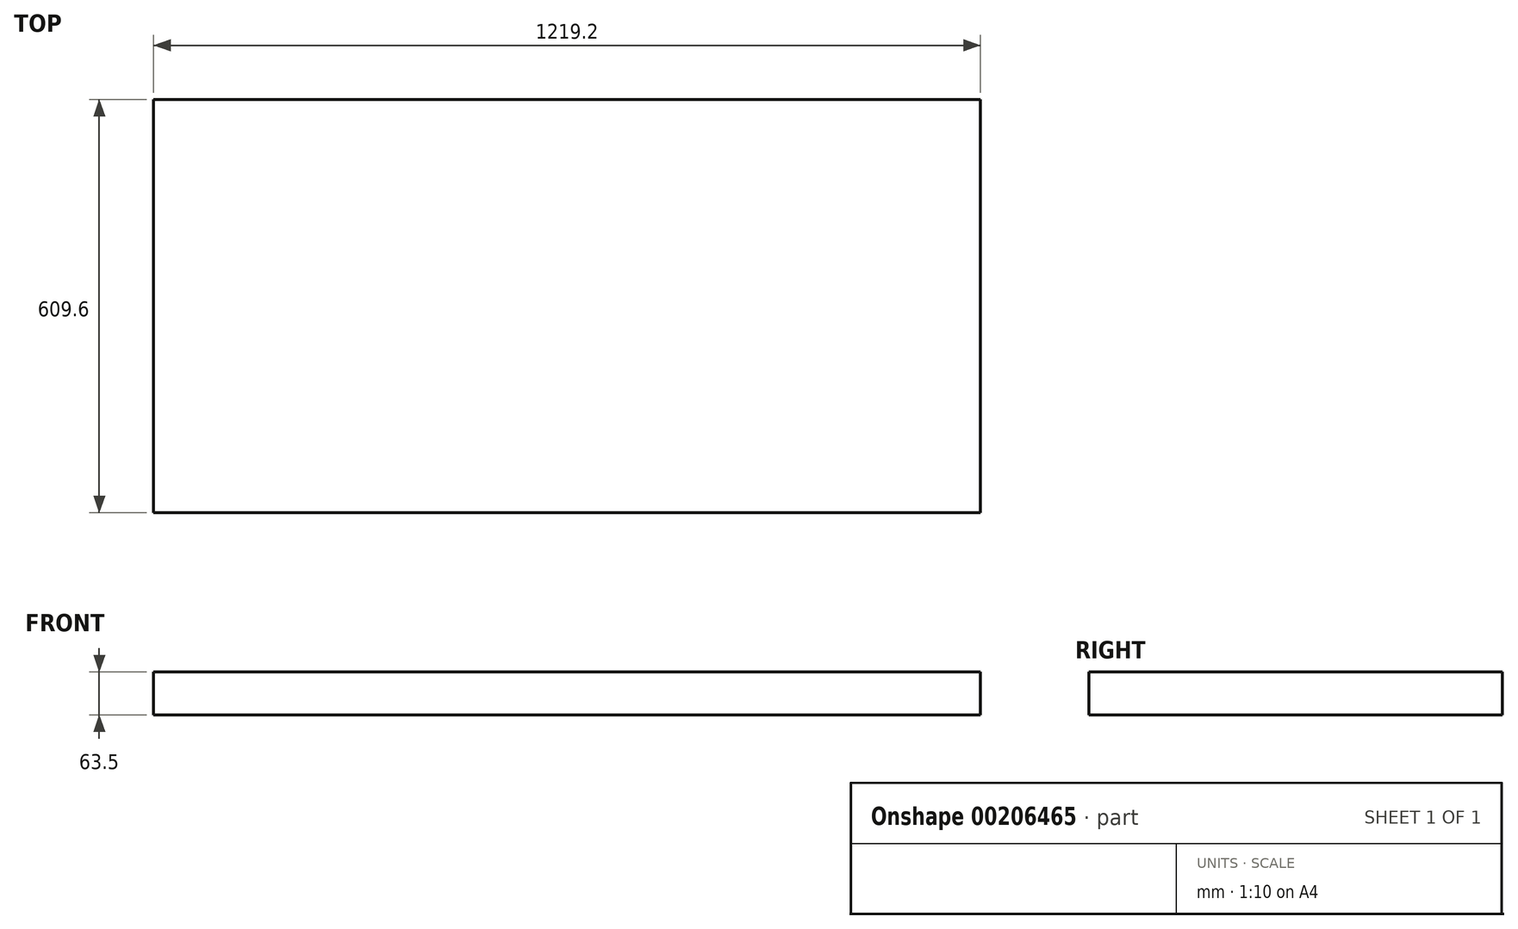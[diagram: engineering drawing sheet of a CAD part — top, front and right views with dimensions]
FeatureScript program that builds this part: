
annotation { "Feature Type Name" : "Feature", "Feature Type Description" : "" }
export const myFeature = defineFeature(function(context is Context, id is Id, definition is map)
    precondition{}
    {
        {
            var Q0;
            Q0=qCreatedBy(makeId("Top.planeOp"),FACE);
            var sketch = newSketch(context, id + "F0", { "sketchPlane" : qUnion([Q0])});
            skLineSegment(sketch, "E0.bottom", {"start": v(609.6, 304.8) * mm, "end": v(-609.6, 304.8) * mm});
            skLineSegment(sketch, "E0.top", {"start": v(609.6, -304.8) * mm, "end": v(-609.6, -304.8) * mm});
            skLineSegment(sketch, "E0.left", {"start": v(609.6, 304.8) * mm, "end": v(609.6, -304.8) * mm});
            skLineSegment(sketch, "E0.right", {"start": v(-609.6, 304.8) * mm, "end": v(-609.6, -304.8) * mm});
            skPoint(sketch, "E0.middle", {"position": v(0, 0) * mm});
            skLineSegment(sketch, "E1.bottom", {"start": v(-609.6, -304.8) * mm, "end": v(-457.2, -304.8) * mm});
            skLineSegment(sketch, "E1.top", {"start": v(-609.6, -152.4) * mm, "end": v(-457.2, -152.4) * mm});
            skLineSegment(sketch, "E1.left", {"start": v(-609.6, -304.8) * mm, "end": v(-609.6, -152.4) * mm});
            skLineSegment(sketch, "E1.right", {"start": v(-457.2, -304.8) * mm, "end": v(-457.2, -152.4) * mm});
            skLineSegment(sketch, "E2.bottom", {"start": v(-609.6, 304.8) * mm, "end": v(-457.2, 304.8) * mm});
            skLineSegment(sketch, "E2.top", {"start": v(-609.6, 152.4) * mm, "end": v(-457.2, 152.4) * mm});
            skLineSegment(sketch, "E2.left", {"start": v(-609.6, 304.8) * mm, "end": v(-609.6, 152.4) * mm});
            skLineSegment(sketch, "E2.right", {"start": v(-457.2, 304.8) * mm, "end": v(-457.2, 152.4) * mm});
            skLineSegment(sketch, "E3.bottom", {"start": v(609.6, 304.8) * mm, "end": v(457.2, 304.8) * mm});
            skLineSegment(sketch, "E3.top", {"start": v(609.6, 152.4) * mm, "end": v(457.2, 152.4) * mm});
            skLineSegment(sketch, "E3.left", {"start": v(609.6, 304.8) * mm, "end": v(609.6, 152.4) * mm});
            skLineSegment(sketch, "E3.right", {"start": v(457.2, 304.8) * mm, "end": v(457.2, 152.4) * mm});
            skLineSegment(sketch, "E4.bottom", {"start": v(609.6, -304.8) * mm, "end": v(457.2, -304.8) * mm});
            skLineSegment(sketch, "E4.top", {"start": v(609.6, -152.4) * mm, "end": v(457.2, -152.4) * mm});
            skLineSegment(sketch, "E4.left", {"start": v(609.6, -304.8) * mm, "end": v(609.6, -152.4) * mm});
            skLineSegment(sketch, "E4.right", {"start": v(457.2, -304.8) * mm, "end": v(457.2, -152.4) * mm});
            skPoint(sketch, "E5", {"position": v(-533.4, -228.6) * mm});
            skPoint(sketch, "E5.positionSnap0", {"position": v(-457.2, -228.6) * mm});
            skPoint(sketch, "E5.positionSnap1", {"position": v(-533.4, -152.4) * mm});
            skPoint(sketch, "E6", {"position": v(-533.4, 228.6) * mm});
            skPoint(sketch, "E6.positionSnap0", {"position": v(-533.4, 304.8) * mm});
            skPoint(sketch, "E6.positionSnap1", {"position": v(-457.2, 228.6) * mm});
            skPoint(sketch, "E7", {"position": v(533.4, 228.6) * mm});
            skPoint(sketch, "E7.positionSnap0", {"position": v(609.6, 228.6) * mm});
            skPoint(sketch, "E7.positionSnap1", {"position": v(533.4, 152.4) * mm});
            skPoint(sketch, "E8", {"position": v(533.4, -228.6) * mm});
            skPoint(sketch, "E8.positionSnap0", {"position": v(533.4, -152.4) * mm});
            skPoint(sketch, "E8.positionSnap1", {"position": v(609.6, -228.6) * mm});
            skLineSegment(sketch, "E9.bottom", {"start": v(-482.6, -279.4) * mm, "end": v(-584.2, -279.4) * mm});
            skLineSegment(sketch, "E9.top", {"start": v(-482.6, -177.8) * mm, "end": v(-584.2, -177.8) * mm});
            skLineSegment(sketch, "E9.left", {"start": v(-482.6, -279.4) * mm, "end": v(-482.6, -177.8) * mm});
            skLineSegment(sketch, "E9.right", {"start": v(-584.2, -279.4) * mm, "end": v(-584.2, -177.8) * mm});
            skLineSegment(sketch, "E10.bottom", {"start": v(-482.6, 177.8) * mm, "end": v(-584.2, 177.8) * mm});
            skLineSegment(sketch, "E10.top", {"start": v(-482.6, 279.4) * mm, "end": v(-584.2, 279.4) * mm});
            skLineSegment(sketch, "E10.left", {"start": v(-482.6, 177.8) * mm, "end": v(-482.6, 279.4) * mm});
            skLineSegment(sketch, "E10.right", {"start": v(-584.2, 177.8) * mm, "end": v(-584.2, 279.4) * mm});
            skLineSegment(sketch, "E11.bottom", {"start": v(584.2, 177.8) * mm, "end": v(482.6, 177.8) * mm});
            skLineSegment(sketch, "E11.top", {"start": v(584.2, 279.4) * mm, "end": v(482.6, 279.4) * mm});
            skLineSegment(sketch, "E11.left", {"start": v(584.2, 177.8) * mm, "end": v(584.2, 279.4) * mm});
            skLineSegment(sketch, "E11.right", {"start": v(482.6, 177.8) * mm, "end": v(482.6, 279.4) * mm});
            skLineSegment(sketch, "E12.bottom", {"start": v(584.2, -279.4) * mm, "end": v(482.6, -279.4) * mm});
            skLineSegment(sketch, "E12.top", {"start": v(584.2, -177.8) * mm, "end": v(482.6, -177.8) * mm});
            skLineSegment(sketch, "E12.left", {"start": v(584.2, -279.4) * mm, "end": v(584.2, -177.8) * mm});
            skLineSegment(sketch, "E12.right", {"start": v(482.6, -279.4) * mm, "end": v(482.6, -177.8) * mm});
            skSolve(sketch);
        }
        {
            var Q0;
            Q0 = qSketchRegion(id + "F0", true);
            var Q1;
            Q1=makeQuery(id+"F0.imprint","IMPRINT",FACE,{"disambiguationData":[TD([[makeQuery(id+"F0.imprint","IMPRINT",EDGE,{"derivedFrom":sQuery(id+"F0.wireOp",EDGE,"E9.bottom")}),-1.0]])]});
            var Q2;
            Q2=makeQuery(id+"F0.imprint","IMPRINT",FACE,{"disambiguationData":[TD([[makeQuery(id+"F0.imprint","IMPRINT",EDGE,{"derivedFrom":sQuery(id+"F0.wireOp",EDGE,"E10.bottom")}),-1.0]])]});
            var Q3;
            Q3=makeQuery(id+"F0.imprint","IMPRINT",FACE,{"disambiguationData":[TD([[makeQuery(id+"F0.imprint","IMPRINT",EDGE,{"derivedFrom":sQuery(id+"F0.wireOp",EDGE,"E11.bottom")}),-1.0]])]});
            var Q4;
            Q4=makeQuery(id+"F0.imprint","IMPRINT",FACE,{"disambiguationData":[TD([[makeQuery(id+"F0.imprint","IMPRINT",EDGE,{"derivedFrom":sQuery(id+"F0.wireOp",EDGE,"E12.bottom")}),-1.0]])]});
            extrude(context, id + "F1", {"entities" : qUnion([Q0, Q1, Q2, Q3, Q4]), "depth" : 63.5 * mm, "offsetDistance" : 25.4 * mm});
        }
    });
